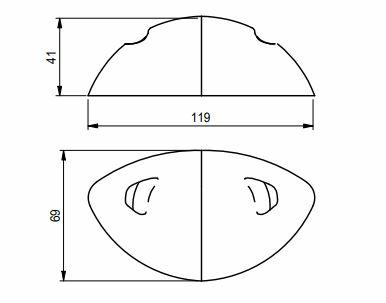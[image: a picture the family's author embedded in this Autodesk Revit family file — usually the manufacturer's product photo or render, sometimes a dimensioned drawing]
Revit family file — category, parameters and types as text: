
# Revit family: R-MBD-488
name_source: partatom
category: Portes
units: mm (PartAtom-declared; Revit-internal decimal feet)

## family parameters
Couper avec des vides une fois chargée = Non
Hôte = Mur
Partagée = Non
Repère de localisation dans la pièce = Oui
Toujours verticalement = Oui

## types (1)
- MBD-488
    1 Vantail = Non
    2 Vantaux = Oui
    A.E.V = non
    Acoustique = non
    Anti-Effraction = non
    Certification = D.A.S. Mode 2 certifié NF
    Code_MAJ = 2303130305MBD488
    Coloris_Chants = BER
    Coloris_Dormant = Hêtre
    Coloris_Face_Cote_Oppose_Ouverture = Prépeint
    Coloris_Face_Cote_Ouverture = Prépeint
    Construction analytique = <Aucun>
    DAS = Oui
    DC Larg Feuillure = 12 mm  [stored 0.0393701 ft]
    DC Pivot Vantail = 60 mm  [stored 0.19685 ft]
    Description = Bloc-porte bois D.A.S. 2 vantaux avec pivots linteaux motorisés encastrés, double action / va-et-vient, EI30, D.A.S. certifié NF, sur huisserie bois sans montant avec fileur
    Définir les propriétés thermiques par = Type schématique
    Ep Profil Pose Tunnel = 118 mm
    Ep Strat Vantail = 1 mm  [stored 0.00328084 ft]
    Ep Vantail = 51 mm  [stored 0.167323 ft]
    Epaisseur_Rainure à brique = 8 mm  [stored 0.0262467 ft]
    Fabricant = MALERBA
    Fiche_Produit = MBD-488
    Fileur = Oui
    Hauteur_Tableau = 2125 mm
    Hauteur_Vantaux_Souhaitée = 2040 mm  [stored 6.69291 ft]
    Jeu_1 = 0 mm  [stored 0 ft]
    Jeu_2 = 0 mm  [stored 0 ft]
    Jeu_Côté_Articulation_Vantail = 8 mm  [stored 0.0262467 ft]
    Jeu_Côté_Fermeture_Vantail = 8 mm  [stored 0.0262467 ft]
    Jeu_Haut = 3 mm  [stored 0.00984252 ft]
    Larg Profil = 58 mm  [stored 0.190289 ft]
    Larg Profil Avec Fileur = 20 mm  [stored 0.0656168 ft]
    Larg Profil Trav = 76 mm  [stored 0.249344 ft]
    Largeur = 0 mm  [stored 0 ft]
    Largeur_Vantail_Semi_Fixe_Souhaitée = 930 mm  [stored 3.05118 ft]
    Largeur_Vantail_Service_Souhaitée = 930 mm  [stored 3.05118 ft]
    Mat APD = Caoutchouc noir
    Mat Parclose = BER 2
    Mat Parclose Métal = Peinture Laquée PMT - Blanc Pur - RAL 9010
    Materiaux_Dominant = Bois
    Modèle = Va et vient
    Montant_VV = Non
    Note d'identification = 2V EI30 DAS - LINTEAU MOTORISE - SANS MONTANT AVEC FILEUR
    Pivot linteau motorisé = Oui
    Profondeur_Rainure à brique = 5 mm  [stored 0.0164042 ft]
    Reference_Commerciale = 2V/DA LINTEAU OP
    Resistance_Feu = EI30
    Sans_Montants = Non
    Sens_Feu = Recto / Verso
    Thermique (W/m2.°K) = 0
    URL = https://www.malerba.fr
    X_Axe Pivot = 88 mm  [stored 0.288714 ft]
    X_DC seuil = 9 mm  [stored 0.0295276 ft]
    X_Inv_DC Larg Feuillure_1V Montant = 0 mm  [stored 0 ft]

note: [stored X ft] marks values corroborated as IEEE doubles in the binary element streams (Revit-internal decimal feet)

## geometry (parser evidence)
native form markers: Blend x14
no freeform markers — native parametric forms only
